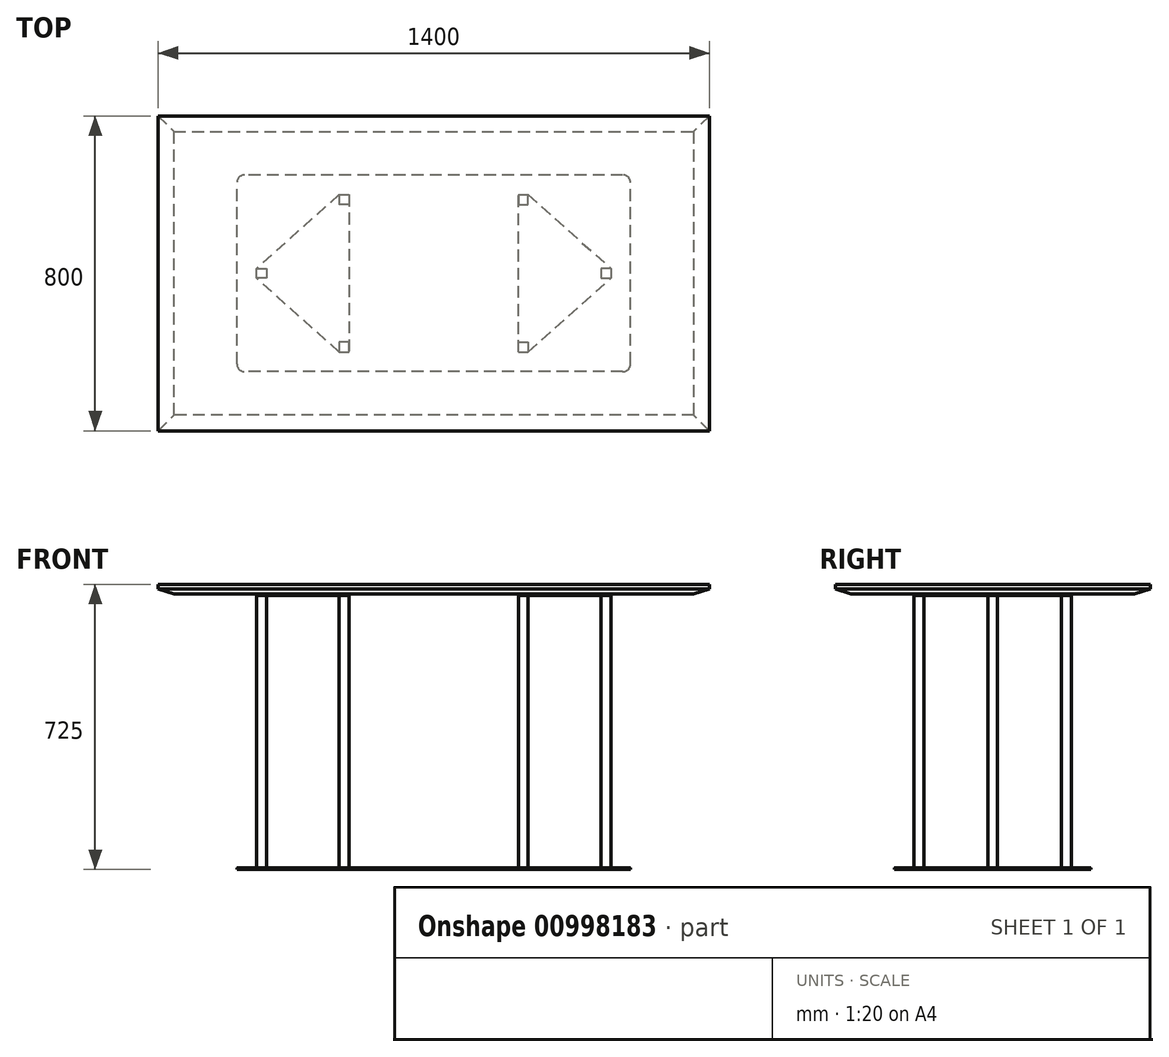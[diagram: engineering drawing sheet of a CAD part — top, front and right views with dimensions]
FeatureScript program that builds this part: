
annotation { "Feature Type Name" : "Feature", "Feature Type Description" : "" }
export const myFeature = defineFeature(function(context is Context, id is Id, definition is map)
    precondition{}
    {
        {
            var Q0;
            Q0=qCreatedBy(makeId("Top.planeOp"),FACE);
            var sketch = newSketch(context, id + "F0", { "sketchPlane" : qUnion([Q0])});
            skLineSegment(sketch, "E0.bottom", {"start": v(0, 0) * mm, "end": v(-1400, 0) * mm, "construction": true});
            skLineSegment(sketch, "E0.top", {"start": v(0, 800) * mm, "end": v(-1400, 800) * mm, "construction": true});
            skLineSegment(sketch, "E0.left", {"start": v(0, 0) * mm, "end": v(0, 800) * mm, "construction": true});
            skLineSegment(sketch, "E0.right", {"start": v(-1400, 0) * mm, "end": v(-1400, 800) * mm, "construction": true});
            skLineSegment(sketch, "E1", {"start": v(-700, 0) * mm, "end": v(-700, 800) * mm, "construction": true});
            skLineSegment(sketch, "E2", {"start": v(-1400, 400) * mm, "end": v(0, 400) * mm, "construction": true});
            skLineSegment(sketch, "E3", {"start": v(0, 400) * mm, "end": v(-250, 400) * mm, "construction": true});
            skLineSegment(sketch, "E4", {"start": v(0, 400) * mm, "end": v(-460, 400) * mm, "construction": true});
            skLineSegment(sketch, "E5", {"start": v(-460, 400) * mm, "end": v(-460, 800) * mm, "construction": true});
            skLineSegment(sketch, "E6", {"start": v(-460, 800) * mm, "end": v(-460, 600) * mm, "construction": true});
            skLineSegment(sketch, "E7", {"start": v(-460, 600) * mm, "end": v(-485, 600) * mm});
            skLineSegment(sketch, "E8", {"start": v(-485, 600) * mm, "end": v(-485, 575) * mm});
            skLineSegment(sketch, "E9", {"start": v(-485, 575) * mm, "end": v(-460, 575) * mm});
            skLineSegment(sketch, "E10", {"start": v(-460, 575) * mm, "end": v(-460, 600) * mm});
            skLineSegment(sketch, "E11", {"start": v(-250, 400) * mm, "end": v(-250, 412.5) * mm});
            skLineSegment(sketch, "E12", {"start": v(-250, 412.5) * mm, "end": v(-275, 412.5) * mm});
            skLineSegment(sketch, "E13", {"start": v(-275, 412.5) * mm, "end": v(-275, 387.5) * mm});
            skLineSegment(sketch, "E14", {"start": v(-275, 387.5) * mm, "end": v(-250, 387.5) * mm});
            skLineSegment(sketch, "E15", {"start": v(-250, 387.5) * mm, "end": v(-250, 412.5) * mm});
            skLineSegment(sketch, "E16.MirrorCS", {"start": v(-460, 200) * mm, "end": v(-485, 200) * mm});
            skLineSegment(sketch, "E17.MirrorCS", {"start": v(-485, 225) * mm, "end": v(-460, 225) * mm});
            skLineSegment(sketch, "E18.MirrorCS", {"start": v(-485, 200) * mm, "end": v(-485, 225) * mm});
            skLineSegment(sketch, "E19.MirrorCS", {"start": v(-460, 225) * mm, "end": v(-460, 200) * mm});
            skLineSegment(sketch, "E20.MirrorCS", {"start": v(-940, 600) * mm, "end": v(-915, 600) * mm});
            skLineSegment(sketch, "E21.MirrorCS", {"start": v(-915, 600) * mm, "end": v(-915, 575) * mm});
            skLineSegment(sketch, "E22.MirrorCS", {"start": v(-915, 575) * mm, "end": v(-940, 575) * mm});
            skLineSegment(sketch, "E23.MirrorCS", {"start": v(-915, 200) * mm, "end": v(-915, 225) * mm});
            skLineSegment(sketch, "E24.MirrorCS", {"start": v(-915, 225) * mm, "end": v(-940, 225) * mm});
            skLineSegment(sketch, "E25.MirrorCS", {"start": v(-940, 200) * mm, "end": v(-915, 200) * mm});
            skLineSegment(sketch, "E26.MirrorCS", {"start": v(-940, 225) * mm, "end": v(-940, 200) * mm});
            skLineSegment(sketch, "E27.MirrorCS", {"start": v(-1150, 412.5) * mm, "end": v(-1125, 412.5) * mm});
            skLineSegment(sketch, "E28.MirrorCS", {"start": v(-1125, 412.5) * mm, "end": v(-1125, 387.5) * mm});
            skLineSegment(sketch, "E29.MirrorCS", {"start": v(-1125, 387.5) * mm, "end": v(-1150, 387.5) * mm});
            skLineSegment(sketch, "E30.MirrorCS", {"start": v(-1150, 387.5) * mm, "end": v(-1150, 412.5) * mm});
            skLineSegment(sketch, "E31", {"start": v(-940, 600) * mm, "end": v(-940, 575) * mm});
            skSolve(sketch);
        }
        {
            var Q0;
            Q0=qSketchRegion(id+"F0",true);
            extrude(context, id + "F1", {"entities" : qUnion([Q0]), "depth" : 700 * mm, "offsetDistance" : 25 * mm});
        }
        {
            var Q0;
            Q0=makeQuery(id+"F1.opExtrude","CAP_FACE",FACE,{"disambiguationData":[OSD([sQuery(id+"F0.wireOp",EDGE,"E7"),sQuery(id+"F0.wireOp",EDGE,"E8"),sQuery(id+"F0.wireOp",EDGE,"E9"),sQuery(id+"F0.wireOp",EDGE,"E10")])],"isStart":false});
            cPlane(context, id + "F2", {"entities" : qUnion([Q0]), "cplaneType" : CPlaneType.OFFSET, "offset" : 0 * mm, "width" : 150 * mm, "height" : 150 * mm});
        }
        {
            var Q0;
            Q0=qCreatedBy(id+"F2.planeOp",FACE);
            var sketch = newSketch(context, id + "F3", { "sketchPlane" : qUnion([Q0])});
            skLineSegment(sketch, "E32.bottom", {"start": v(0, 0) * mm, "end": v(-1400, 0) * mm, "construction": true});
            skLineSegment(sketch, "E32.top", {"start": v(0, 800) * mm, "end": v(-1400, 800) * mm, "construction": true});
            skLineSegment(sketch, "E32.left", {"start": v(0, 0) * mm, "end": v(0, 800) * mm, "construction": true});
            skLineSegment(sketch, "E32.right", {"start": v(-1400, 0) * mm, "end": v(-1400, 800) * mm, "construction": true});
            skLineSegment(sketch, "E33", {"start": v(-700, 0) * mm, "end": v(-700, 400) * mm, "construction": true});
            skLineSegment(sketch, "E34", {"start": v(0, 400) * mm, "end": v(-250, 400) * mm, "construction": true});
            skLineSegment(sketch, "E35", {"start": v(-250, 400) * mm, "end": v(-250, 412.5) * mm});
            skLineSegment(sketch, "E36", {"start": v(-700, 400) * mm, "end": v(-485, 400) * mm, "construction": true});
            skLineSegment(sketch, "E37", {"start": v(-485, 400) * mm, "end": v(-485, 600) * mm});
            skLineSegment(sketch, "E38", {"start": v(-485, 600) * mm, "end": v(-460, 600) * mm});
            skLineSegment(sketch, "E39", {"start": v(-460, 600) * mm, "end": v(-250, 412.5) * mm});
            skLineSegment(sketch, "E40.MirrorCS", {"start": v(-460, 200) * mm, "end": v(-250, 387.5) * mm});
            skLineSegment(sketch, "E41.MirrorCS", {"start": v(-250, 400) * mm, "end": v(-250, 387.5) * mm});
            skLineSegment(sketch, "E42.MirrorCS", {"start": v(-485, 200) * mm, "end": v(-460, 200) * mm});
            skLineSegment(sketch, "E43.MirrorCS", {"start": v(-485, 400) * mm, "end": v(-485, 200) * mm});
            skLineSegment(sketch, "E44.MirrorCS", {"start": v(-940, 600) * mm, "end": v(-1150, 412.5) * mm});
            skLineSegment(sketch, "E45.MirrorCS", {"start": v(-1150, 400) * mm, "end": v(-1150, 412.5) * mm});
            skLineSegment(sketch, "E46.MirrorCS", {"start": v(-1150, 400) * mm, "end": v(-1150, 387.5) * mm});
            skLineSegment(sketch, "E47.MirrorCS", {"start": v(-940, 200) * mm, "end": v(-1150, 387.5) * mm});
            skLineSegment(sketch, "E48.MirrorCS", {"start": v(-915, 400) * mm, "end": v(-915, 600) * mm});
            skLineSegment(sketch, "E49.MirrorCS", {"start": v(-915, 400) * mm, "end": v(-915, 200) * mm});
            skLineSegment(sketch, "E50.MirrorCS", {"start": v(-915, 200) * mm, "end": v(-940, 200) * mm});
            skLineSegment(sketch, "E51.MirrorCS", {"start": v(-915, 600) * mm, "end": v(-940, 600) * mm});
            skSolve(sketch);
        }
        {
            var Q0;
            Q0=qSketchRegion(id+"F3",true);
            extrude(context, id + "F4", {"entities" : qUnion([Q0]), "oppositeDirection" : true, "depth" : 3 * mm, "offsetDistance" : 25 * mm});
        }
        {
            var Q0;
            Q0=makeQuery(id+"F4.opExtrude","CAP_FACE",FACE,{"disambiguationData":[OSD([sQuery(id+"F3.wireOp",EDGE,"E44.MirrorCS"),sQuery(id+"F3.wireOp",EDGE,"E45.MirrorCS"),sQuery(id+"F3.wireOp",EDGE,"E46.MirrorCS"),sQuery(id+"F3.wireOp",EDGE,"E47.MirrorCS"),sQuery(id+"F3.wireOp",EDGE,"E48.MirrorCS"),sQuery(id+"F3.wireOp",EDGE,"E49.MirrorCS"),sQuery(id+"F3.wireOp",EDGE,"E50.MirrorCS"),sQuery(id+"F3.wireOp",EDGE,"E51.MirrorCS")])],"isStart":true});
            cPlane(context, id + "F5", {"entities" : qUnion([Q0]), "cplaneType" : CPlaneType.OFFSET, "offset" : 0 * mm, "width" : 150 * mm, "height" : 150 * mm});
        }
        {
            var Q0;
            Q0=qCreatedBy(id+"F5.planeOp",FACE);
            var sketch = newSketch(context, id + "F6", { "sketchPlane" : qUnion([Q0])});
            skLineSegment(sketch, "E52.bottom", {"start": v(0, 0) * mm, "end": v(-1400, 0) * mm});
            skLineSegment(sketch, "E52.top", {"start": v(0, 800) * mm, "end": v(-1400, 800) * mm});
            skLineSegment(sketch, "E52.left", {"start": v(0, 0) * mm, "end": v(0, 800) * mm});
            skLineSegment(sketch, "E52.right", {"start": v(-1400, 0) * mm, "end": v(-1400, 800) * mm});
            skSolve(sketch);
        }
        {
            var Q0;
            Q0=qSketchRegion(id+"F6",true);
            extrude(context, id + "F7", {"entities" : qUnion([Q0]), "depth" : 25 * mm, "offsetDistance" : 25 * mm});
        }
        {
            var Q0;
            Q0=makeQuery(id+"F7.opExtrude","CAP_FACE",FACE,{"disambiguationData":[OSD([sQuery(id+"F6.wireOp",EDGE,"E52.bottom"),sQuery(id+"F6.wireOp",EDGE,"E52.top"),sQuery(id+"F6.wireOp",EDGE,"E52.left"),sQuery(id+"F6.wireOp",EDGE,"E52.right")])],"isStart":true});
            chamfer(context, id + "F8", {"entities" : qUnion([Q0]), "chamferType" : ChamferType.TWO_OFFSETS, "width1" : 40 * mm, "oppositeDirection" : false, "width2" : 12.5 * mm, "tangentPropagation" : true});
        }
        {
            var Q0;
            Q0=makeQuery(id+"F1.opExtrude","CAP_FACE",FACE,{"disambiguationData":[OSD([sQuery(id+"F0.wireOp",EDGE,"E23.MirrorCS"),sQuery(id+"F0.wireOp",EDGE,"E24.MirrorCS"),sQuery(id+"F0.wireOp",EDGE,"E25.MirrorCS"),sQuery(id+"F0.wireOp",EDGE,"E26.MirrorCS")])],"isStart":true});
            cPlane(context, id + "F9", {"entities" : qUnion([Q0]), "cplaneType" : CPlaneType.OFFSET, "offset" : 5 * mm, "oppositeDirection" : true, "width" : 150 * mm, "height" : 150 * mm});
        }
        {
            var Q0;
            Q0=qCreatedBy(id+"F9.planeOp",FACE);
            var sketch = newSketch(context, id + "F10", { "sketchPlane" : qUnion([Q0])});
            skLineSegment(sketch, "E53", {"start": v(0, 0) * mm, "end": v(-200, 0) * mm, "construction": true});
            skLineSegment(sketch, "E54", {"start": v(-200, 0) * mm, "end": v(-200, -150) * mm, "construction": true});
            skLineSegment(sketch, "E55.bottom", {"start": v(-200, -150) * mm, "end": v(-1200, -150) * mm});
            skLineSegment(sketch, "E55.top", {"start": v(-200, -650) * mm, "end": v(-1200, -650) * mm});
            skLineSegment(sketch, "E55.left", {"start": v(-200, -150) * mm, "end": v(-200, -650) * mm});
            skLineSegment(sketch, "E55.right", {"start": v(-1200, -150) * mm, "end": v(-1200, -650) * mm});
            skSolve(sketch);
        }
        {
            var Q0;
            Q0 = qSketchRegion(id + "F10", true);
            extrude(context, id + "F11", {"entities" : qUnion([Q0]), "depth" : 5 * mm, "offsetDistance" : 25 * mm});
        }
        {
            var Q0;
            Q0=makeQuery(id+"F11.opExtrude","SWEPT_EDGE",EDGE,{"disambiguationData":[OSD([sQuery(id+"F10.wireOp",EDGE,"E55.bottom"),sQuery(id+"F10.wireOp",EDGE,"E55.right")])]});
            var Q1;
            Q1=makeQuery(id+"F11.opExtrude","SWEPT_EDGE",EDGE,{"disambiguationData":[OSD([sQuery(id+"F10.wireOp",EDGE,"E55.top"),sQuery(id+"F10.wireOp",EDGE,"E55.right")])]});
            var Q2;
            Q2=makeQuery(id+"F11.opExtrude","SWEPT_EDGE",EDGE,{"disambiguationData":[OSD([sQuery(id+"F10.wireOp",EDGE,"E55.bottom"),sQuery(id+"F10.wireOp",EDGE,"E55.left")])]});
            var Q3;
            Q3=makeQuery(id+"F11.opExtrude","SWEPT_EDGE",EDGE,{"disambiguationData":[OSD([sQuery(id+"F10.wireOp",EDGE,"E55.top"),sQuery(id+"F10.wireOp",EDGE,"E55.left")])]});
            fillet(context, id + "F12", {"entities" : qUnion([Q0, Q1, Q2, Q3]), "radius" : 20 * mm, "tangentPropagation" : true, "allowEdgeOverflow" : false});
        }
        {
            var Q0;
            Q0=makeQuery(id+"F11.opExtrude","CAP_EDGE",EDGE,{"disambiguationData":[OSD([sQuery(id+"F10.wireOp",EDGE,"E55.bottom")])],"isStart":true});
            var Q1;
            Q1=makeQuery(id+"F11.opExtrude","CAP_EDGE",EDGE,{"disambiguationData":[OSD([sQuery(id+"F10.wireOp",EDGE,"E55.left")])],"isStart":true});
            var Q2;
            {var subQ0=sQuery(id+"F10.wireOp",EDGE,"E55.left");var subQ1=sQuery(id+"F10.wireOp",EDGE,"E55.top");Q2=makeQuery(id+"F12.opFillet","BLEND_EDGE",EDGE,{"blendedFrom":[makeQuery(id+"F11.opExtrude","SWEPT_EDGE",EDGE,{"disambiguationData":[OSD([subQ1,subQ0])]}),makeQuery(id+"F11.opExtrude","CAP_FACE",FACE,{"disambiguationData":[OSD([sQuery(id+"F10.wireOp",EDGE,"E55.bottom"),subQ1,subQ0,sQuery(id+"F10.wireOp",EDGE,"E55.right")])],"isStart":true})],"blendedInto":[makeQuery(id+"F11.opExtrude","CAP_FACE",FACE,{"disambiguationData":[OSD([sQuery(id+"F10.wireOp",EDGE,"E55.bottom"),subQ1,subQ0,sQuery(id+"F10.wireOp",EDGE,"E55.right")])],"isStart":true})]});}
            var Q3;
            Q3=makeQuery(id+"F11.opExtrude","CAP_EDGE",EDGE,{"disambiguationData":[OSD([sQuery(id+"F10.wireOp",EDGE,"E55.top")])],"isStart":true});
            var Q4;
            {var subQ0=sQuery(id+"F10.wireOp",EDGE,"E55.right");var subQ1=sQuery(id+"F10.wireOp",EDGE,"E55.top");Q4=makeQuery(id+"F12.opFillet","BLEND_EDGE",EDGE,{"blendedFrom":[makeQuery(id+"F11.opExtrude","SWEPT_EDGE",EDGE,{"disambiguationData":[OSD([subQ1,subQ0])]}),makeQuery(id+"F11.opExtrude","CAP_FACE",FACE,{"disambiguationData":[OSD([sQuery(id+"F10.wireOp",EDGE,"E55.bottom"),subQ1,sQuery(id+"F10.wireOp",EDGE,"E55.left"),subQ0])],"isStart":true})],"blendedInto":[makeQuery(id+"F11.opExtrude","CAP_FACE",FACE,{"disambiguationData":[OSD([sQuery(id+"F10.wireOp",EDGE,"E55.bottom"),subQ1,sQuery(id+"F10.wireOp",EDGE,"E55.left"),subQ0])],"isStart":true})]});}
            var Q5;
            Q5=makeQuery(id+"F11.opExtrude","CAP_EDGE",EDGE,{"disambiguationData":[OSD([sQuery(id+"F10.wireOp",EDGE,"E55.right")])],"isStart":true});
            var Q6;
            {var subQ0=sQuery(id+"F10.wireOp",EDGE,"E55.right");var subQ1=sQuery(id+"F10.wireOp",EDGE,"E55.bottom");Q6=makeQuery(id+"F12.opFillet","BLEND_EDGE",EDGE,{"blendedFrom":[makeQuery(id+"F11.opExtrude","SWEPT_EDGE",EDGE,{"disambiguationData":[OSD([subQ1,subQ0])]}),makeQuery(id+"F11.opExtrude","CAP_FACE",FACE,{"disambiguationData":[OSD([subQ1,sQuery(id+"F10.wireOp",EDGE,"E55.top"),sQuery(id+"F10.wireOp",EDGE,"E55.left"),subQ0])],"isStart":true})],"blendedInto":[makeQuery(id+"F11.opExtrude","CAP_FACE",FACE,{"disambiguationData":[OSD([subQ1,sQuery(id+"F10.wireOp",EDGE,"E55.top"),sQuery(id+"F10.wireOp",EDGE,"E55.left"),subQ0])],"isStart":true})]});}
            fillet(context, id + "F13", {"entities" : qUnion([Q0, Q1, Q2, Q3, Q4, Q5, Q6]), "radius" : 3 * mm, "tangentPropagation" : true, "allowEdgeOverflow" : false});
        }
    });
